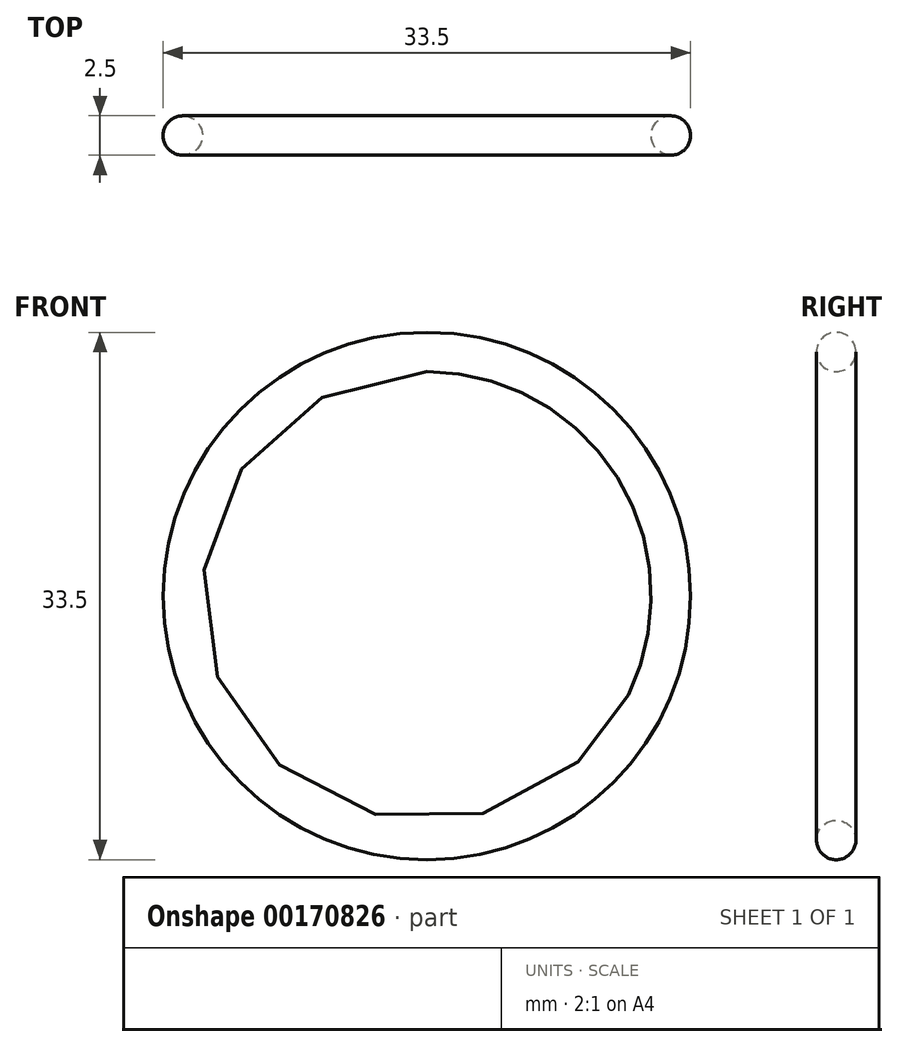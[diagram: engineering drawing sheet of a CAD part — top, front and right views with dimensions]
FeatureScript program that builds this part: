
annotation { "Feature Type Name" : "Feature", "Feature Type Description" : "" }
export const myFeature = defineFeature(function(context is Context, id is Id, definition is map)
    precondition{}
    {
        {
            var Q0;
            Q0=qCreatedBy(makeId("Top.planeOp"),FACE);
            var sketch = newSketch(context, id + "F0", { "sketchPlane" : qUnion([Q0])});
            skCircle(sketch, "E0", {"center": v(0, 0) * mm, "radius": 1.25 * mm});
            skLineSegment(sketch, "E1", {"start": v(15.5, 21.7) * mm, "end": v(15.5, -26.93) * mm, "construction": true});
            skSolve(sketch);
        }
        {
            var Q0;
            Q0 = qSketchRegion(id + "F0", true);
            var Q1;
            Q1=sQuery(id+"F0.wireOp",EDGE,"E1");
            revolve(context, id + "F1", {"entities" : qUnion([Q0]), "axis" : qUnion([Q1]), "revolveType" : RevolveType.FULL});
        }
    });
